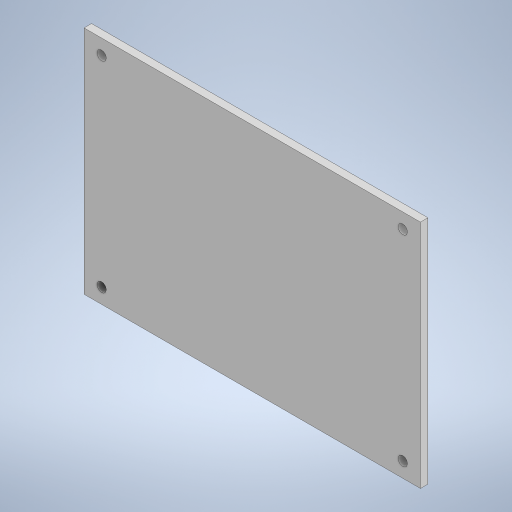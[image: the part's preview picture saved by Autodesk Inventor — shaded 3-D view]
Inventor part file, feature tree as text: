
AUTODESK INVENTOR PART (.ipt)
format: ipt  version: 2023.1 (Build 271208000, 208)  size: 198,656 bytes
history: native  units: mm
features: other x1, extrude x1, sketch x1
ambient origin geometry x8: Origin, YZ Plane, XZ Plane, XY Plane, X Axis, Y Axis, Z Axis, Center Point
bodies: Body1 (feature_tree)
feature tree (3):
  other  "솔리드1"
  extrude  "돌출1"  Depth=71.6mm
  sketch  "스케치1"
